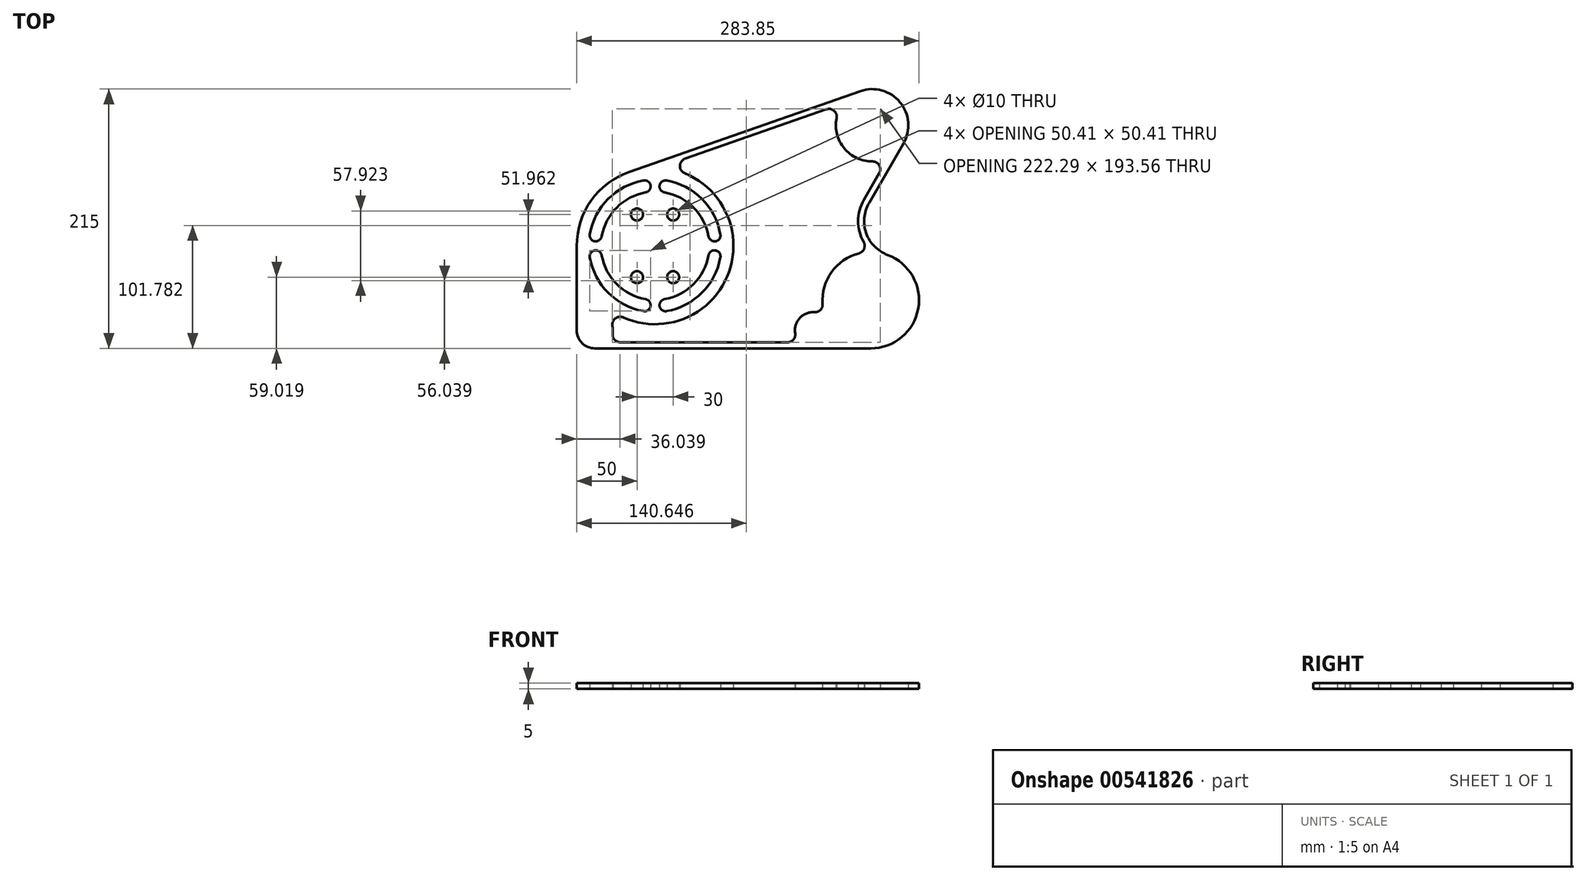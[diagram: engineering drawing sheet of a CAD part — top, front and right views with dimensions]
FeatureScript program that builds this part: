
annotation { "Feature Type Name" : "Feature", "Feature Type Description" : "" }
export const myFeature = defineFeature(function(context is Context, id is Id, definition is map)
    precondition{}
    {
        {
            var Q0;
            Q0=qCreatedBy(makeId("Top.planeOp"),FACE);
            var sketch = newSketch(context, id + "F0", { "sketchPlane" : qUnion([Q0])});
            skCircle(sketch, "E0", {"center": v(0, 0) * mm, "radius": 60 * mm});
            skCircle(sketch, "E1", {"center": v(180, 100) * mm, "radius": 25 * mm});
            skCircle(sketch, "E2", {"center": v(178.85, -45) * mm, "radius": 35 * mm});
            skArc(sketch, "E3.0", {"start": v(-21.45, 61.36) * mm, "mid": v(-53, 37.62) * mm, "end": v(-65, 0) * mm});
            skArc(sketch, "E4.0", {"start": v(150.57, 105.82) * mm, "mid": v(156.9, 80.86) * mm, "end": v(180.24, 70) * mm});
            skArc(sketch, "E5.0", {"start": v(168.94, -6.25) * mm, "mid": v(146.34, -21.7) * mm, "end": v(138.96, -48.05) * mm});
            skLineSegment(sketch, "E6", {"start": v(-65, 0) * mm, "end": v(-65, -70) * mm});
            skLineSegment(sketch, "E7", {"start": v(178.85, -85) * mm, "end": v(-50, -85) * mm});
            skLineSegment(sketch, "E8", {"start": v(-21.45, 61.36) * mm, "end": v(170.1, 128.32) * mm});
            skLineSegment(sketch, "E9", {"start": v(205.98, 85) * mm, "end": v(177.43, 35.55) * mm});
            skArc(sketch, "E10", {"start": v(177.43, 35.55) * mm, "mid": v(175.17, 10.42) * mm, "end": v(192.88, -7.54) * mm});
            skLineSegment(sketch, "E11.0", {"start": v(24.98, 72.3) * mm, "end": v(142.05, 113.22) * mm});
            skArc(sketch, "E12.0", {"start": v(173.1, 38.05) * mm, "mid": v(168.41, 20.67) * mm, "end": v(172.98, 3.26) * mm});
            skLineSegment(sketch, "E12.1", {"start": v(185.92, 60.25) * mm, "end": v(173.1, 38.05) * mm});
            skArc(sketch, "E13.trimOffspring", {"start": v(205.98, 85) * mm, "mid": v(203.1, 119.14) * mm, "end": v(170.1, 128.32) * mm});
            skCircle(sketch, "E14", {"center": v(131, -70) * mm, "radius": 4.25 * mm});
            skArc(sketch, "E15", {"start": v(132.03, -55.04) * mm, "mid": v(119.9, -59.9) * mm, "end": v(116.2, -72.44) * mm});
            skCircle(sketch, "E16", {"center": v(-50, -70) * mm, "radius": 4.25 * mm});
            skArc(sketch, "E17", {"start": v(-35.2, -72.44) * mm, "mid": v(-35, -69.6) * mm, "end": v(-35.35, -66.76) * mm});
            skArc(sketch, "E18", {"start": v(-26.37, -59.4) * mm, "mid": v(-33.12, -60.32) * mm, "end": v(-35.35, -66.76) * mm});
            skLineSegment(sketch, "E19.trimOffspring", {"start": v(109.79, -80) * mm, "end": v(-28.79, -80) * mm});
            skArc(sketch, "E20.trimOffspring", {"start": v(178.85, -85) * mm, "mid": v(218.2, -52.13) * mm, "end": v(192.88, -7.54) * mm});
            skPoint(sketch, "E21.visualSharp", {"position": v(3.8, 64.89) * mm});
            skArc(sketch, "E21.filletArc", {"start": v(24.98, 72.3) * mm, "mid": v(20.62, 66.33) * mm, "end": v(24.66, 60.14) * mm});
            skPoint(sketch, "E22.visualSharp", {"position": v(179.5, -5) * mm});
            skArc(sketch, "E22.filletArc", {"start": v(168.94, -6.25) * mm, "mid": v(173.3, -2.5) * mm, "end": v(172.98, 3.26) * mm});
            skPoint(sketch, "E23.visualSharp", {"position": v(193.36, 73.14) * mm});
            skArc(sketch, "E23.filletArc", {"start": v(185.92, 60.25) * mm, "mid": v(185.9, 66.77) * mm, "end": v(180.24, 70) * mm});
            skPoint(sketch, "E24.visualSharp", {"position": v(119.82, -80) * mm});
            skArc(sketch, "E24.filletArc", {"start": v(109.79, -80) * mm, "mid": v(114.74, -77.7) * mm, "end": v(116.2, -72.44) * mm});
            skPoint(sketch, "E25.visualSharp", {"position": v(-38.82, -80) * mm});
            skArc(sketch, "E25.filletArc", {"start": v(-35.2, -72.44) * mm, "mid": v(-33.74, -77.7) * mm, "end": v(-28.79, -80) * mm});
            skPoint(sketch, "E26.visualSharp", {"position": v(156.1, 118.13) * mm});
            skArc(sketch, "E26.filletArc", {"start": v(150.57, 105.82) * mm, "mid": v(148.45, 111.99) * mm, "end": v(142.05, 113.22) * mm});
            skPoint(sketch, "E27.visualSharp", {"position": v(141.48, -59.26) * mm});
            skArc(sketch, "E27.filletArc", {"start": v(132.03, -55.04) * mm, "mid": v(137.1, -53.13) * mm, "end": v(138.96, -48.05) * mm});
            skCircle(sketch, "E28", {"center": v(30, 0) * mm, "radius": 5 * mm});
            skCircle(sketch, "E29.1.0", {"center": v(15, 25.98) * mm, "radius": 5 * mm});
            skCircle(sketch, "E29.2.0", {"center": v(-15, 25.98) * mm, "radius": 5 * mm});
            skCircle(sketch, "E29.3.0", {"center": v(-30, 0) * mm, "radius": 5 * mm});
            skCircle(sketch, "E29.4.0", {"center": v(-15, -25.98) * mm, "radius": 5 * mm});
            skCircle(sketch, "E29.5.0", {"center": v(15, -25.98) * mm, "radius": 5 * mm});
            skCircle(sketch, "E30", {"center": v(0, 0) * mm, "radius": 50 * mm, "construction": true});
            skArc(sketch, "E31.0", {"start": v(-54.16, -9.55) * mm, "mid": v(-38.9, -38.9) * mm, "end": v(-9.55, -54.16) * mm});
            skArc(sketch, "E32.0", {"start": v(-7.81, 44.32) * mm, "mid": v(-31.82, 31.82) * mm, "end": v(-44.32, 7.81) * mm});
            skArc(sketch, "E33.0", {"start": v(-9.55, 54.16) * mm, "mid": v(-38.9, 38.9) * mm, "end": v(-54.16, 9.55) * mm, "construction": true});
            skLineSegment(sketch, "E34", {"start": v(49.24, 8.68) * mm, "end": v(0, 0) * mm, "construction": true});
            skLineSegment(sketch, "E35", {"start": v(0, 0) * mm, "end": v(50, 0) * mm, "construction": true});
            skArc(sketch, "E36", {"start": v(9.55, 54.16) * mm, "mid": v(3.76, 50.1) * mm, "end": v(7.81, 44.32) * mm});
            skLineSegment(sketch, "E37", {"start": v(8.68, 49.24) * mm, "end": v(0, 0) * mm, "construction": true});
            skLineSegment(sketch, "E38", {"start": v(0, 0) * mm, "end": v(0, 50) * mm, "construction": true});
            skArc(sketch, "E39.MirrorC", {"start": v(-44.32, 7.81) * mm, "mid": v(-50.1, 3.76) * mm, "end": v(-54.16, 9.55) * mm});
            skArc(sketch, "E40.MirrorC", {"start": v(-9.55, 54.16) * mm, "mid": v(-3.76, 50.1) * mm, "end": v(-7.81, 44.32) * mm});
            skArc(sketch, "E41.MirrorC", {"start": v(44.32, 7.81) * mm, "mid": v(50.1, 3.76) * mm, "end": v(54.16, 9.55) * mm});
            skArc(sketch, "E42.MirrorC", {"start": v(44.32, -7.81) * mm, "mid": v(50.1, -3.76) * mm, "end": v(54.16, -9.55) * mm});
            skArc(sketch, "E43.MirrorC", {"start": v(9.55, -54.16) * mm, "mid": v(3.76, -50.1) * mm, "end": v(7.81, -44.32) * mm});
            skArc(sketch, "E44.MirrorC", {"start": v(-9.55, -54.16) * mm, "mid": v(-3.76, -50.1) * mm, "end": v(-7.81, -44.32) * mm});
            skArc(sketch, "E45.MirrorC", {"start": v(-44.32, -7.81) * mm, "mid": v(-50.1, -3.76) * mm, "end": v(-54.16, -9.55) * mm});
            skArc(sketch, "E46.trimOffspring", {"start": v(-44.32, -7.81) * mm, "mid": v(-31.82, -31.82) * mm, "end": v(-7.81, -44.32) * mm});
            skArc(sketch, "E47.trimOffspring", {"start": v(-54.16, -9.55) * mm, "mid": v(-38.9, -38.9) * mm, "end": v(-9.55, -54.16) * mm, "construction": true});
            skArc(sketch, "E48.trimOffspring", {"start": v(7.81, -44.32) * mm, "mid": v(31.82, -31.82) * mm, "end": v(44.32, -7.81) * mm});
            skArc(sketch, "E49.trimOffspring", {"start": v(9.55, -54.16) * mm, "mid": v(38.9, -38.9) * mm, "end": v(54.16, -9.55) * mm, "construction": true});
            skArc(sketch, "E50.trimOffspring", {"start": v(54.16, 9.55) * mm, "mid": v(38.9, 38.9) * mm, "end": v(9.55, 54.16) * mm, "construction": true});
            skArc(sketch, "E51.trimOffspring", {"start": v(45, 0) * mm, "mid": v(34.47, 28.93) * mm, "end": v(7.81, 44.32) * mm});
            skArc(sketch, "E52.trimOffspring", {"start": v(9.55, -54.16) * mm, "mid": v(38.9, -38.9) * mm, "end": v(54.16, -9.55) * mm});
            skArc(sketch, "E53.trimOffspring", {"start": v(54.16, 9.55) * mm, "mid": v(38.9, 38.9) * mm, "end": v(9.55, 54.16) * mm});
            skArc(sketch, "E54.trimOffspring", {"start": v(-9.55, 54.16) * mm, "mid": v(-38.9, 38.9) * mm, "end": v(-54.16, 9.55) * mm});
            skPoint(sketch, "E55.visualSharp", {"position": v(-65, -85) * mm});
            skArc(sketch, "E55.filletArc", {"start": v(-65, -70) * mm, "mid": v(-60.6, -80.6) * mm, "end": v(-50, -85) * mm});
            skArc(sketch, "E56.trimOffspring", {"start": v(-26.37, -59.4) * mm, "mid": v(59.78, -25.52) * mm, "end": v(24.66, 60.14) * mm});
            skSolve(sketch);
        }
        {
            var Q0;
            Q0=makeQuery(id+"F0.imprint","IMPRINT",FACE,{"disambiguationData":[TD([[makeQuery(id+"F0.imprint","IMPRINT",EDGE,{"derivedFrom":sQuery(id+"F0.wireOp",EDGE,"E0")}),-1.0]])]});
            var Q1;
            Q1=makeQuery(id+"F0.imprint","IMPRINT",FACE,{"disambiguationData":[TD([[makeQuery(id+"F0.imprint","IMPRINT",EDGE,{"derivedFrom":sQuery(id+"F0.wireOp",EDGE,"E4.0")}),-1.0]])]});
            var Q2;
            Q2=makeQuery(id+"F0.imprint","IMPRINT",FACE,{"disambiguationData":[TD([[makeQuery(id+"F0.imprint","IMPRINT",EDGE,{"derivedFrom":sQuery(id+"F0.wireOp",EDGE,"E42.MirrorC")}),-1.0]])]});
            var Q3;
            Q3=makeQuery(id+"F0.imprint","IMPRINT",FACE,{"disambiguationData":[TD([[makeQuery(id+"F0.imprint","IMPRINT",EDGE,{"derivedFrom":sQuery(id+"F0.wireOp",EDGE,"E2")}),1.0]])]});
            var Q4;
            {var subQ0=sQuery(id+"F0.wireOp",EDGE,"E41.MirrorC");Q4=makeQuery(id+"F0.imprint","IMPRINT",FACE,{"disambiguationData":[TD([[makeQuery(id+"F0.imprint","IMPRINT",EDGE,{"derivedFrom":subQ0}),1.0]])]});}
            var Q5;
            Q5=makeQuery(id+"F0.imprint","IMPRINT",FACE,{"disambiguationData":[TD([[makeQuery(id+"F0.imprint","IMPRINT",EDGE,{"derivedFrom":sQuery(id+"F0.wireOp",EDGE,"E1")}),1.0]])]});
            var Q6;
            Q6=makeQuery(id+"F0.imprint","IMPRINT",FACE,{"disambiguationData":[TD([[makeQuery(id+"F0.imprint","IMPRINT",EDGE,{"derivedFrom":sQuery(id+"F0.wireOp",EDGE,"E29.3.0")}),1.0]])]});
            var Q7;
            Q7=makeQuery(id+"F0.imprint","IMPRINT",FACE,{"disambiguationData":[TD([[makeQuery(id+"F0.imprint","IMPRINT",EDGE,{"derivedFrom":sQuery(id+"F0.wireOp",EDGE,"E31.0")}),1.0]])]});
            var Q8;
            Q8=makeQuery(id+"F0.imprint","IMPRINT",FACE,{"disambiguationData":[TD([[makeQuery(id+"F0.imprint","IMPRINT",EDGE,{"derivedFrom":sQuery(id+"F0.wireOp",EDGE,"E32.0")}),-1.0]])]});
            var Q9;
            Q9=makeQuery(id+"F0.imprint","IMPRINT",FACE,{"disambiguationData":[TD([[makeQuery(id+"F0.imprint","IMPRINT",EDGE,{"derivedFrom":sQuery(id+"F0.wireOp",EDGE,"E0")}),1.0]])]});
            var Q10;
            Q10=makeQuery(id+"F0.imprint","IMPRINT",FACE,{"disambiguationData":[TD([[makeQuery(id+"F0.imprint","IMPRINT",EDGE,{"derivedFrom":sQuery(id+"F0.wireOp",EDGE,"E16")}),1.0]])]});
            var Q11;
            Q11=makeQuery(id+"F0.imprint","IMPRINT",FACE,{"disambiguationData":[TD([[makeQuery(id+"F0.imprint","IMPRINT",EDGE,{"derivedFrom":sQuery(id+"F0.wireOp",EDGE,"E28")}),1.0]])]});
            var Q12;
            Q12=makeQuery(id+"F0.imprint","IMPRINT",FACE,{"disambiguationData":[TD([[makeQuery(id+"F0.imprint","IMPRINT",EDGE,{"derivedFrom":sQuery(id+"F0.wireOp",EDGE,"E14")}),1.0]])]});
            var Q13;
            Q13=makeQuery(id+"F0.imprint","IMPRINT",FACE,{"disambiguationData":[TD([[makeQuery(id+"F0.imprint","IMPRINT",EDGE,{"derivedFrom":sQuery(id+"F0.wireOp",EDGE,"E29.1.0")}),1.0]])]});
            var Q14;
            Q14=makeQuery(id+"F0.imprint","IMPRINT",FACE,{"disambiguationData":[TD([[makeQuery(id+"F0.imprint","IMPRINT",EDGE,{"derivedFrom":sQuery(id+"F0.wireOp",EDGE,"E29.2.0")}),1.0]])]});
            var Q15;
            Q15=makeQuery(id+"F0.imprint","IMPRINT",FACE,{"disambiguationData":[TD([[makeQuery(id+"F0.imprint","IMPRINT",EDGE,{"derivedFrom":sQuery(id+"F0.wireOp",EDGE,"E29.4.0")}),1.0]])]});
            var Q16;
            Q16=makeQuery(id+"F0.imprint","IMPRINT",FACE,{"disambiguationData":[TD([[makeQuery(id+"F0.imprint","IMPRINT",EDGE,{"derivedFrom":sQuery(id+"F0.wireOp",EDGE,"E29.5.0")}),1.0]])]});
            extrude(context, id + "F1", {"entities" : qUnion([Q0, Q1, Q2, Q3, Q4, Q5, Q6, Q7, Q8, Q9, Q10, Q11, Q12, Q13, Q14, Q15, Q16]), "depth" : 5 * mm, "offsetDistance" : 25 * mm});
        }
    });
